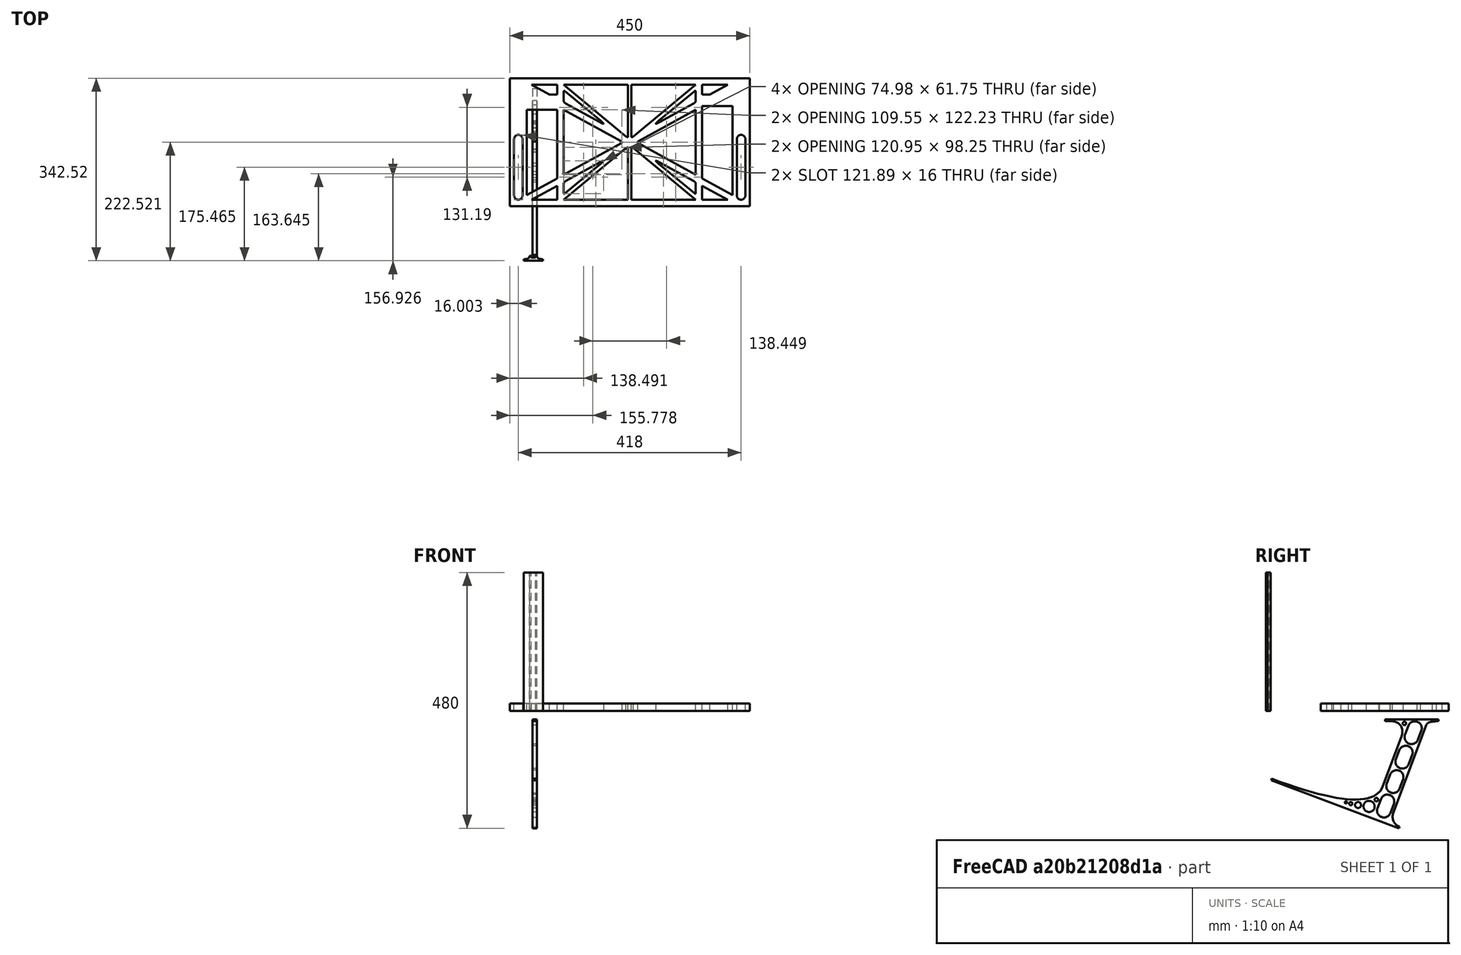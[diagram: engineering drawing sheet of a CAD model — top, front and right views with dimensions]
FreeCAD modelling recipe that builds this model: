
FCSTD DOCUMENT  (FreeCAD 0.19R0.19.2)
Label: laptopStand078
License: All rights reserved
LicenseURL: http://en.wikipedia.org/wiki/All_rights_reserved
objects: Sketcher::SketchObject×3, Part::Extrusion×3
note: 6 computed .brp shape members not serialized (recipe doc carries the construction recipe); baked Part::Feature solids carry a one-line shape summary decoded from their .brp

FEATURE [Sketcher::SketchObject] Sketch
  FullyConstrained = false
  sketch-geometry (180):
    g0: LineSegment StartX=-10.9272 StartY=-82.7794 StartZ=0 EndX=46.0728 EndY=-51.4823 EndZ=0
    g1: LineSegment StartX=366.073 StartY=-91.7794 StartZ=0 EndX=318.073 EndY=-65.424 EndZ=0
    g2: LineSegment StartX=-10.9272 StartY=77.3346 StartZ=0 EndX=-10.9272 EndY=-82.7794 EndZ=0
    g3: LineSegment StartX=375.073 StartY=-82.7794 StartZ=0 EndX=375.073 EndY=83.9235 EndZ=0
    g4: LineSegment StartX=-1.92719 StartY=-91.7794 StartZ=0 EndX=46.0728 EndY=-91.7794 EndZ=0
    g5: LineSegment StartX=318.073 StartY=124.221 StartZ=0 EndX=366.073 EndY=124.221 EndZ=0
    g6: LineSegment StartX=306.073 StartY=124.221 StartZ=0 EndX=189.124 EndY=27.0628 EndZ=0
    g7: LineSegment StartX=58.0728 StartY=-91.7794 StartZ=0 EndX=175.022 EndY=5.37834 EndZ=0
    g8: LineSegment StartX=175.022 StartY=27.0628 StartZ=0 EndX=58.0728 EndY=124.221 EndZ=0
    g9: LineSegment StartX=189.124 StartY=5.37834 StartZ=0 EndX=306.073 EndY=-91.7794 EndZ=0
    g10: LineSegment StartX=306.073 StartY=77.3346 StartZ=0 EndX=306.073 EndY=-44.8935 EndZ=0
    g11: LineSegment StartX=318.073 StartY=83.9235 StartZ=0 EndX=318.073 EndY=-51.4823 EndZ=0
    g12: LineSegment StartX=318.073 StartY=-51.4823 StartZ=0 EndX=375.073 EndY=-82.7794 EndZ=0
    g13: LineSegment StartX=318.073 StartY=-65.424 StartZ=0 EndX=318.073 EndY=-91.7794 EndZ=0
    g14: LineSegment StartX=318.073 StartY=-91.7794 StartZ=0 EndX=366.073 EndY=-91.7794 EndZ=0
    g15: LineSegment StartX=58.0728 StartY=-44.8935 StartZ=0 EndX=58.0728 EndY=77.3346 EndZ=0
    g16: LineSegment StartX=46.0728 StartY=-65.424 StartZ=0 EndX=-1.92719 EndY=-91.7794 EndZ=0
    g17: LineSegment StartX=46.0728 StartY=-65.424 StartZ=0 EndX=46.0728 EndY=-91.7794 EndZ=0
    g18: LineSegment StartX=46.0728 StartY=77.3346 StartZ=0 EndX=46.0728 EndY=-51.4823 EndZ=0
    g19: LineSegment StartX=-42.9272 StartY=136.221 StartZ=0 EndX=-42.9272 EndY=-103.779 EndZ=0
    g20: LineSegment StartX=407.073 StartY=136.221 StartZ=0 EndX=407.073 EndY=-103.779 EndZ=0
    g21: LineSegment StartX=179.022 StartY=27.0628 StartZ=0 EndX=179.022 EndY=124.221 EndZ=0
    g22: LineSegment StartX=185.124 StartY=27.0628 StartZ=0 EndX=185.124 EndY=124.221 EndZ=0
    g23: ArcOfCircle CenterX=-26.9272 CenterY=22.1087 CenterZ=0 NormalX=0 NormalY=0 NormalZ=1 AngleXU=0 Radius=8 StartAngle=1e-16 EndAngle=3.14159
    g24: ArcOfCircle CenterX=-26.9272 CenterY=-83.7794 CenterZ=0 NormalX=0 NormalY=0 NormalZ=1 AngleXU=0 Radius=8 StartAngle=3.14159 EndAngle=6.28319
    g25: LineSegment StartX=-34.9272 StartY=22.1087 StartZ=0 EndX=-34.9272 EndY=-83.7794 EndZ=0
    g26: LineSegment StartX=-18.9272 StartY=22.1087 StartZ=0 EndX=-18.9272 EndY=-83.7794 EndZ=0
    g27: LineSegment StartX=185.124 StartY=-91.7794 StartZ=0 EndX=306.073 EndY=-91.7794 EndZ=0
    g28: LineSegment StartX=179.022 StartY=-91.7794 StartZ=0 EndX=58.0728 EndY=-91.7794 EndZ=0
    g29: LineSegment StartX=306.073 StartY=124.221 StartZ=0 EndX=185.124 EndY=124.221 EndZ=0
    g30: LineSegment StartX=179.022 StartY=124.221 StartZ=0 EndX=58.0728 EndY=124.221 EndZ=0
    g31: ArcOfCircle CenterX=391.073 CenterY=22.1087 CenterZ=0 NormalX=0 NormalY=0 NormalZ=1 AngleXU=0 Radius=8 StartAngle=-4.4e-15 EndAngle=3.14159
    g32: LineSegment StartX=399.073 StartY=22.1087 StartZ=0 EndX=399.073 EndY=-83.7794 EndZ=0
    g33: LineSegment StartX=383.073 StartY=22.1087 StartZ=0 EndX=383.073 EndY=-83.7794 EndZ=0
    g34: ArcOfCircle CenterX=391.073 CenterY=-83.7794 CenterZ=0 NormalX=0 NormalY=0 NormalZ=1 AngleXU=0 Radius=8 StartAngle=3.14159 EndAngle=6.28319
    g35: Circle CenterX=175.022 CenterY=27.0628 CenterZ=0 NormalX=0 NormalY=0 NormalZ=1 AngleXU=0 Radius=1
    g36: Circle CenterX=179.022 CenterY=24.8665 CenterZ=0 NormalX=0 NormalY=0 NormalZ=1 AngleXU=0 Radius=1
    g37: Circle CenterX=179.022 CenterY=27.0628 CenterZ=0 NormalX=0 NormalY=0 NormalZ=1 AngleXU=0 Radius=1
    g38: BSplineCurve PolesCount=3 KnotsCount=2 Degree=2 IsPeriodic=0
    g39: GeomPoint X=175.022 Y=27.0628 Z=0
    g40: GeomPoint X=179.022 Y=27.0628 Z=0
    g41: Circle CenterX=189.124 CenterY=27.0628 CenterZ=0 NormalX=0 NormalY=0 NormalZ=1 AngleXU=0 Radius=1
    g42: Circle CenterX=185.124 CenterY=24.8665 CenterZ=0 NormalX=0 NormalY=0 NormalZ=1 AngleXU=0 Radius=1
    g43: Circle CenterX=185.124 CenterY=27.0628 CenterZ=0 NormalX=0 NormalY=0 NormalZ=1 AngleXU=0 Radius=1
    g44: BSplineCurve PolesCount=3 KnotsCount=2 Degree=2 IsPeriodic=0
    g45: GeomPoint X=189.124 Y=27.0628 Z=0
    g46: GeomPoint X=185.124 Y=27.0628 Z=0
    g47: Circle CenterX=175.022 CenterY=5.37834 CenterZ=0 NormalX=0 NormalY=0 NormalZ=1 AngleXU=0 Radius=1
    g48: Circle CenterX=179.022 CenterY=7.57463 CenterZ=0 NormalX=0 NormalY=0 NormalZ=1 AngleXU=0 Radius=1
    g49: Circle CenterX=179.022 CenterY=5.34704 CenterZ=0 NormalX=0 NormalY=0 NormalZ=1 AngleXU=0 Radius=1
    g50: BSplineCurve PolesCount=3 KnotsCount=2 Degree=2 IsPeriodic=0
    g51: GeomPoint X=175.022 Y=5.37834 Z=0
    g52: GeomPoint X=179.022 Y=5.34704 Z=0
    g53: Circle CenterX=189.124 CenterY=5.37834 CenterZ=0 NormalX=0 NormalY=0 NormalZ=1 AngleXU=0 Radius=1
    g54: Circle CenterX=185.124 CenterY=7.57463 CenterZ=0 NormalX=0 NormalY=0 NormalZ=1 AngleXU=0 Radius=1
    g55: Circle CenterX=185.124 CenterY=5.34704 CenterZ=0 NormalX=0 NormalY=0 NormalZ=1 AngleXU=0 Radius=1
    g56: BSplineCurve PolesCount=3 KnotsCount=2 Degree=2 IsPeriodic=0
    g57: GeomPoint X=189.124 Y=5.37834 Z=0
    g58: GeomPoint X=185.124 Y=5.34704 Z=0
    g59: LineSegment StartX=179.022 StartY=5.34704 StartZ=0 EndX=179.022 EndY=-91.7794 EndZ=0
    g60: LineSegment StartX=185.124 StartY=-91.7794 StartZ=0 EndX=185.124 EndY=5.34704 EndZ=0
    g61: Circle CenterX=165.871 CenterY=18.1458 CenterZ=0 NormalX=0 NormalY=0 NormalZ=1 AngleXU=0 Radius=1
    g62: Circle CenterX=169.377 CenterY=16.2206 CenterZ=0 NormalX=0 NormalY=0 NormalZ=1 AngleXU=0 Radius=1
    g63: Circle CenterX=165.871 CenterY=14.2954 CenterZ=0 NormalX=0 NormalY=0 NormalZ=1 AngleXU=0 Radius=1
    g64: BSplineCurve PolesCount=3 KnotsCount=2 Degree=2 IsPeriodic=0
    g65: GeomPoint X=165.871 Y=18.1458 Z=0
    g66: GeomPoint X=165.871 Y=14.2954 Z=0
    g67: Circle CenterX=198.275 CenterY=18.1458 CenterZ=0 NormalX=0 NormalY=0 NormalZ=1 AngleXU=0 Radius=1
    g68: Circle CenterX=194.768 CenterY=16.2206 CenterZ=0 NormalX=0 NormalY=0 NormalZ=1 AngleXU=0 Radius=1
    g69: Circle CenterX=198.275 CenterY=14.2954 CenterZ=0 NormalX=0 NormalY=0 NormalZ=1 AngleXU=0 Radius=1
    g70: BSplineCurve PolesCount=3 KnotsCount=2 Degree=2 IsPeriodic=0
    g71: GeomPoint X=198.275 Y=18.1458 Z=0
    g72: GeomPoint X=198.275 Y=14.2954 Z=0
    g73: LineSegment StartX=165.871 StartY=18.1458 StartZ=0 EndX=58.0728 EndY=77.3346 EndZ=0
    g74: LineSegment StartX=58.0728 StartY=-44.8935 StartZ=0 EndX=165.871 EndY=14.2954 EndZ=0
    g75: LineSegment StartX=198.275 StartY=18.1458 StartZ=0 EndX=306.073 EndY=77.3346 EndZ=0
    g76: LineSegment StartX=198.275 StartY=14.2954 StartZ=0 EndX=306.073 EndY=-44.8935 EndZ=0
    g77: LineSegment StartX=407.073 StartY=-103.779 StartZ=0 EndX=-42.9272 EndY=-103.779 EndZ=0
    g78: LineSegment StartX=407.073 StartY=136.221 StartZ=0 EndX=-42.9272 EndY=136.221 EndZ=0
    g79: LineSegment StartX=46.0728 StartY=77.3346 StartZ=0 EndX=-10.9272 EndY=77.3346 EndZ=0
    g80: LineSegment StartX=46.0728 StartY=105.865 StartZ=0 EndX=31.5028 EndY=105.865 EndZ=0
    g81: LineSegment StartX=46.0728 StartY=124.221 StartZ=0 EndX=46.0728 EndY=105.865 EndZ=0
    g82: LineSegment StartX=-1.92719 StartY=124.221 StartZ=0 EndX=31.5028 EndY=105.865 EndZ=0
    g83: LineSegment StartX=46.0728 StartY=124.221 StartZ=0 EndX=-1.92719 EndY=124.221 EndZ=0
    g84: LineSegment StartX=318.073 StartY=83.9235 StartZ=0 EndX=375.073 EndY=83.9235 EndZ=0
    g85: LineSegment StartX=318.073 StartY=105.865 StartZ=0 EndX=332.643 EndY=105.865 EndZ=0
    g86: LineSegment StartX=332.643 StartY=105.865 StartZ=0 EndX=366.073 EndY=124.221 EndZ=0
    g87: LineSegment StartX=318.073 StartY=124.221 StartZ=0 EndX=318.073 EndY=105.865 EndZ=0
    g88: Circle CenterX=125.607 CenterY=54.1951 CenterZ=0 NormalX=0 NormalY=0 NormalZ=1 AngleXU=0 Radius=1
    g89: Circle CenterX=139.632 CenterY=46.4944 CenterZ=0 NormalX=0 NormalY=0 NormalZ=1 AngleXU=0 Radius=1
    g90: Circle CenterX=127.326 CenterY=56.7187 CenterZ=0 NormalX=0 NormalY=0 NormalZ=1 AngleXU=0 Radius=1
    g91: BSplineCurve PolesCount=3 KnotsCount=2 Degree=2 IsPeriodic=0
    g92: GeomPoint X=125.607 Y=54.1951 Z=0
    g93: GeomPoint X=127.326 Y=56.7187 Z=0
    g94: Circle CenterX=236.821 CenterY=56.7187 CenterZ=0 NormalX=0 NormalY=0 NormalZ=1 AngleXU=0 Radius=1
    g95: Circle CenterX=224.513 CenterY=46.4944 CenterZ=0 NormalX=0 NormalY=0 NormalZ=1 AngleXU=0 Radius=1
    g96: Circle CenterX=238.538 CenterY=54.1951 CenterZ=0 NormalX=0 NormalY=0 NormalZ=1 AngleXU=0 Radius=1
    g97: BSplineCurve PolesCount=3 KnotsCount=2 Degree=2 IsPeriodic=0
    g98: GeomPoint X=236.821 Y=56.7187 Z=0
    g99: GeomPoint X=238.538 Y=54.1951 Z=0
    g100: Circle CenterX=238.538 CenterY=-21.7539 CenterZ=0 NormalX=0 NormalY=0 NormalZ=1 AngleXU=0 Radius=1
    g101: Circle CenterX=224.513 CenterY=-14.0532 CenterZ=0 NormalX=0 NormalY=0 NormalZ=1 AngleXU=0 Radius=1
    g102: Circle CenterX=236.821 CenterY=-24.2775 CenterZ=0 NormalX=0 NormalY=0 NormalZ=1 AngleXU=0 Radius=1
    g103: BSplineCurve PolesCount=3 KnotsCount=2 Degree=2 IsPeriodic=0
    g104: GeomPoint X=238.538 Y=-21.7539 Z=0
    g105: GeomPoint X=236.821 Y=-24.2775 Z=0
    g106: Circle CenterX=125.607 CenterY=-21.7539 CenterZ=0 NormalX=0 NormalY=0 NormalZ=1 AngleXU=0 Radius=1
    g107: Circle CenterX=139.632 CenterY=-14.0532 CenterZ=0 NormalX=0 NormalY=0 NormalZ=1 AngleXU=0 Radius=1
    g108: Circle CenterX=127.325 CenterY=-24.2775 CenterZ=0 NormalX=0 NormalY=0 NormalZ=1 AngleXU=0 Radius=1
    g109: BSplineCurve PolesCount=3 KnotsCount=2 Degree=2 IsPeriodic=0
    g110: GeomPoint X=125.607 Y=-21.7539 Z=0
    g111: GeomPoint X=127.325 Y=-24.2775 Z=0
    g112: Circle CenterX=302.996 CenterY=111.695 CenterZ=0 NormalX=0 NormalY=0 NormalZ=1 AngleXU=0 Radius=1
    g113: Circle CenterX=306.073 CenterY=114.251 CenterZ=0 NormalX=0 NormalY=0 NormalZ=1 AngleXU=0 Radius=1
    g114: Circle CenterX=306.073 CenterY=110.251 CenterZ=0 NormalX=0 NormalY=0 NormalZ=1 AngleXU=0 Radius=1
    g115: BSplineCurve PolesCount=3 KnotsCount=2 Degree=2 IsPeriodic=0
    g116: GeomPoint X=302.996 Y=111.695 Z=0
    g117: GeomPoint X=306.073 Y=110.251 Z=0
    g118: Circle CenterX=306.073 CenterY=95.2763 CenterZ=0 NormalX=0 NormalY=0 NormalZ=1 AngleXU=0 Radius=1
    g119: Circle CenterX=306.073 CenterY=91.2763 CenterZ=0 NormalX=0 NormalY=0 NormalZ=1 AngleXU=0 Radius=1
    g120: Circle CenterX=302.567 CenterY=89.3511 CenterZ=0 NormalX=0 NormalY=0 NormalZ=1 AngleXU=0 Radius=1
    g121: BSplineCurve PolesCount=3 KnotsCount=2 Degree=2 IsPeriodic=0
    g122: GeomPoint X=306.073 Y=95.2763 Z=0
    g123: GeomPoint X=302.567 Y=89.3511 Z=0
    g124: LineSegment StartX=306.073 StartY=110.251 StartZ=0 EndX=306.073 EndY=95.2763 EndZ=0
    g125: LineSegment StartX=302.996 StartY=111.695 StartZ=0 EndX=236.821 EndY=56.7187 EndZ=0
    g126: LineSegment StartX=238.538 StartY=54.1951 StartZ=0 EndX=302.567 EndY=89.3511 EndZ=0
    g127: Circle CenterX=61.1496 CenterY=111.695 CenterZ=0 NormalX=0 NormalY=0 NormalZ=1 AngleXU=0 Radius=1
    g128: Circle CenterX=58.0728 CenterY=114.251 CenterZ=0 NormalX=0 NormalY=0 NormalZ=1 AngleXU=0 Radius=1
    g129: Circle CenterX=58.0728 CenterY=110.251 CenterZ=0 NormalX=0 NormalY=0 NormalZ=1 AngleXU=0 Radius=1
    g130: BSplineCurve PolesCount=3 KnotsCount=2 Degree=2 IsPeriodic=0
    g131: GeomPoint X=61.1496 Y=111.695 Z=0
    g132: GeomPoint X=58.0728 Y=110.251 Z=0
    g133: Circle CenterX=61.5791 CenterY=89.3511 CenterZ=0 NormalX=0 NormalY=0 NormalZ=1 AngleXU=0 Radius=1
    g134: Circle CenterX=58.0728 CenterY=91.2763 CenterZ=0 NormalX=0 NormalY=0 NormalZ=1 AngleXU=0 Radius=1
    g135: Circle CenterX=58.0728 CenterY=95.2763 CenterZ=0 NormalX=0 NormalY=0 NormalZ=1 AngleXU=0 Radius=1
    g136: BSplineCurve PolesCount=3 KnotsCount=2 Degree=2 IsPeriodic=0
    g137: GeomPoint X=61.5791 Y=89.3511 Z=0
    g138: GeomPoint X=58.0728 Y=95.2763 Z=0
    g139: LineSegment StartX=58.0728 StartY=110.251 StartZ=0 EndX=58.0728 EndY=95.2763 EndZ=0
    g140: LineSegment StartX=61.1496 StartY=111.695 StartZ=0 EndX=127.326 EndY=56.7187 EndZ=0
    g141: LineSegment StartX=125.607 StartY=54.1951 StartZ=0 EndX=61.5791 EndY=89.3511 EndZ=0
    g142: Circle CenterX=61.5791 CenterY=-56.9099 CenterZ=0 NormalX=0 NormalY=0 NormalZ=1 AngleXU=0 Radius=1
    g143: Circle CenterX=58.0728 CenterY=-58.8351 CenterZ=0 NormalX=0 NormalY=0 NormalZ=1 AngleXU=0 Radius=1
    g144: Circle CenterX=58.0728 CenterY=-62.8351 CenterZ=0 NormalX=0 NormalY=0 NormalZ=1 AngleXU=0 Radius=1
    g145: BSplineCurve PolesCount=3 KnotsCount=2 Degree=2 IsPeriodic=0
    g146: GeomPoint X=61.5791 Y=-56.9099 Z=0
    g147: GeomPoint X=58.0728 Y=-62.8351 Z=0
    g148: Circle CenterX=58.0728 CenterY=-77.8102 CenterZ=0 NormalX=0 NormalY=0 NormalZ=1 AngleXU=0 Radius=1
    g149: Circle CenterX=58.0728 CenterY=-81.8102 CenterZ=0 NormalX=0 NormalY=0 NormalZ=1 AngleXU=0 Radius=1
    g150: Circle CenterX=61.1496 CenterY=-79.2541 CenterZ=0 NormalX=0 NormalY=0 NormalZ=1 AngleXU=0 Radius=1
    g151: BSplineCurve PolesCount=3 KnotsCount=2 Degree=2 IsPeriodic=0
    g152: GeomPoint X=58.0728 Y=-77.8102 Z=0
    g153: GeomPoint X=61.1496 Y=-79.2541 Z=0
    g154: LineSegment StartX=58.0728 StartY=-62.8351 StartZ=0 EndX=58.0728 EndY=-77.8102 EndZ=0
    g155: LineSegment StartX=61.1496 StartY=-79.2541 StartZ=0 EndX=127.325 EndY=-24.2775 EndZ=0
    g156: LineSegment StartX=125.607 StartY=-21.7539 StartZ=0 EndX=61.5791 EndY=-56.9099 EndZ=0
    g157: Circle CenterX=302.567 CenterY=-56.9099 CenterZ=0 NormalX=0 NormalY=0 NormalZ=1 AngleXU=0 Radius=1
    g158: Circle CenterX=306.073 CenterY=-58.8351 CenterZ=0 NormalX=0 NormalY=0 NormalZ=1 AngleXU=0 Radius=1
    g159: Circle CenterX=306.073 CenterY=-62.8351 CenterZ=0 NormalX=0 NormalY=0 NormalZ=1 AngleXU=0 Radius=1
    g160: BSplineCurve PolesCount=3 KnotsCount=2 Degree=2 IsPeriodic=0
    g161: GeomPoint X=302.567 Y=-56.9099 Z=0
    g162: GeomPoint X=306.073 Y=-62.8351 Z=0
    g163: Circle CenterX=302.996 CenterY=-79.2541 CenterZ=0 NormalX=0 NormalY=0 NormalZ=1 AngleXU=0 Radius=1
    g164: Circle CenterX=306.073 CenterY=-81.8102 CenterZ=0 NormalX=0 NormalY=0 NormalZ=1 AngleXU=0 Radius=1
    g165: Circle CenterX=306.073 CenterY=-77.8102 CenterZ=0 NormalX=0 NormalY=0 NormalZ=1 AngleXU=0 Radius=1
    g166: BSplineCurve PolesCount=3 KnotsCount=2 Degree=2 IsPeriodic=0
    g167: GeomPoint X=302.996 Y=-79.2541 Z=0
    g168: GeomPoint X=306.073 Y=-77.8102 Z=0
    g169: LineSegment StartX=306.073 StartY=-62.8351 StartZ=0 EndX=306.073 EndY=-77.8102 EndZ=0
    g170: LineSegment StartX=302.996 StartY=-79.2541 StartZ=0 EndX=236.821 EndY=-24.2775 EndZ=0
    g171: LineSegment StartX=238.538 StartY=-21.7539 StartZ=0 EndX=302.567 EndY=-56.9099 EndZ=0
    g172: LineSegment StartX=58.0728 StartY=-91.7794 StartZ=0 EndX=63.9135 EndY=-91.7794 EndZ=0
    g173: LineSegment StartX=58.0728 StartY=-91.7794 StartZ=0 EndX=61.6457 EndY=-88.8112 EndZ=0
    g174: LineSegment StartX=179.022 StartY=-91.7794 StartZ=0 EndX=171.895 EndY=-91.7794 EndZ=0
    g175: LineSegment StartX=179.022 StartY=-91.7794 StartZ=0 EndX=179.022 EndY=-85.8163 EndZ=0
    g176: LineSegment StartX=185.124 StartY=-91.7794 StartZ=0 EndX=185.124 EndY=-86.2028 EndZ=0
    g177: LineSegment StartX=185.124 StartY=-91.7794 StartZ=0 EndX=191.747 EndY=-91.7794 EndZ=0
    g178: LineSegment StartX=306.073 StartY=-91.7794 StartZ=0 EndX=298.776 EndY=-91.7794 EndZ=0
    g179: LineSegment StartX=306.073 StartY=-91.7794 StartZ=0 EndX=299.888 EndY=-86.6416 EndZ=0
  constraints (316):
    c: Horizontal(g4)
    c: Horizontal(g5)
    c: Coincident(g11,g12)
    c: Coincident(g13,g1)
    c: Tangent(g11,g13)
    c: Coincident(g17,g16)
    c: Coincident(g0,g18)
    c: Block(g8)
    c: Block(g6)
    c: Block(g12)
    c: Block(g3)
    c: Block(g1)
    c: Block(g13)
    c: Block(g9)
    c: Block(g7)
    c: Block(g17)
    c: Block(g16)
    c: Block(g0)
    c: Block(g2)
    c: Block(g10)
    c: Block(g5)
    c: Block(g14)
    c: Block(g4)
    c: Vertical(g19)
    c: Vertical(g20)
    c: Block(g20)
    c: Block(g19)
    c: Vertical(g21)
    c: Vertical(g22)
    c: Block(g21)
    c: Block(g22)
    c: Tangent(g23,g26) = 1.5708
    c: Tangent(g23,g25) = -1.5708
    c: Tangent(g25,g24) = -1.5708
    c: Tangent(g26,g24) = 1.5708
    c: Vertical(g25)
    c: Equal(g23,g24)
    c: Block(g26)
    c: Block(g25)
    c: Coincident(g27,g9)
    c: Horizontal(g27)
    c: Coincident(g28,g7)
    c: Horizontal(g28)
    c: Coincident(g29,g6)
    c: Coincident(g29,g22)
    c: Horizontal(g29)
    c: Coincident(g30,g21)
    c: Coincident(g30,g8)
    c: Horizontal(g30)
    c: Tangent(g31,g32) = 1.5708
    c: Tangent(g32,g34) = 1.5708
    c: Equal(g31,g34)
    c: Coincident(g33,g31)
    c: Coincident(g33,g34)
    c: Block(g32)
    c: Block(g33)
    c: Coincident(g38,g8)
    c: Weight(g35) = 1
    c: Equal(g35,g36)
    c: Equal(g35,g37)
    c: Coincident(g38,g21)
    c: InternalAlignment(g35,g38)
    c: InternalAlignment(g36,g38)
    c: InternalAlignment(g37,g38)
    c: InternalAlignment(g39,g38)
    c: InternalAlignment(g40,g38)
    c: Coincident(g44,g6)
    c: Weight(g41) = 1
    c: Equal(g41,g42)
    c: Equal(g41,g43)
    c: Coincident(g44,g22)
    c: InternalAlignment(g41,g44)
    c: InternalAlignment(g42,g44)
    c: InternalAlignment(g43,g44)
    c: InternalAlignment(g45,g44)
    c: InternalAlignment(g46,g44)
    c: Block(g44)
    c: Block(g38)
    c: Coincident(g50,g7)
    c: Weight(g47) = 1
    c: Equal(g47,g48)
    c: Equal(g47,g49)
    c: InternalAlignment(g47,g50)
    c: InternalAlignment(g48,g50)
    c: InternalAlignment(g49,g50)
    c: InternalAlignment(g51,g50)
    c: InternalAlignment(g52,g50)
    c: Weight(g53) = 1
    c: Equal(g53,g54)
    c: Equal(g53,g55)
    c: InternalAlignment(g53,g56)
    c: InternalAlignment(g54,g56)
    c: InternalAlignment(g55,g56)
    c: InternalAlignment(g57,g56)
    c: InternalAlignment(g58,g56)
    c: Block(g56)
    c: Block(g50)
    c: Coincident(g59,g50)
    c: Coincident(g59,g28)
    c: Vertical(g59)
    c: Coincident(g60,g27)
    c: Coincident(g60,g56)
    c: Vertical(g60)
    c: Weight(g61) = 1
    c: Equal(g61,g62)
    c: Equal(g61,g63)
    c: InternalAlignment(g61,g64)
    c: InternalAlignment(g62,g64)
    c: InternalAlignment(g63,g64)
    c: InternalAlignment(g65,g64)
    c: InternalAlignment(g66,g64)
    c: Weight(g67) = 1
    c: Equal(g67,g68)
    c: Equal(g67,g69)
    c: InternalAlignment(g67,g70)
    c: InternalAlignment(g68,g70)
    c: InternalAlignment(g69,g70)
    c: InternalAlignment(g71,g70)
    c: InternalAlignment(g72,g70)
    c: Block(g64)
    c: Block(g70)
    c: Coincident(g73,g64)
    c: Coincident(g73,g15)
    c: Coincident(g74,g15)
    c: Coincident(g74,g64)
    c: Coincident(g75,g70)
    c: Coincident(g75,g10)
    c: Coincident(g76,g70)
    c: Coincident(g76,g10)
    c: Block(g15)
    c: Coincident(g77,g20)
    c: Coincident(g77,g19)
    c: Horizontal(g77)
    c: Distance(g77) = 450
    c: Coincident(g78,g20)
    c: Coincident(g78,g19)
    c: Horizontal(g78)
    c: Horizontal(g79)
    c: Coincident(g18,g79)
    c: Horizontal(g80)
    c: Vertical(g81)
    c: Block(g81)
    c: Block(g80)
    c: Block(g79)
    c: Distance(g81) = 18.3554
    c: Coincident(g83,g81)
    c: Coincident(g83,g82)
    c: Horizontal(g83)
    c: Block(g83)
    c: Block(g82)
    c: Coincident(g80,g82)
    c: Coincident(g2,g79)
    c: Coincident(g84,g11)
    c: Horizontal(g84)
    c: Horizontal(g85)
    c: Block(g84)
    c: Coincident(g86,g5)
    c: Coincident(g87,g5)
    c: Coincident(g87,g85)
    c: Vertical(g87)
    c: Block(g87)
    c: Coincident(g85,g86)
    c: Block(g86)
    c: Coincident(g3,g84)
    c: Weight(g88) = 1
    c: Equal(g88,g89)
    c: Equal(g88,g90)
    c: InternalAlignment(g88,g91)
    c: InternalAlignment(g89,g91)
    c: InternalAlignment(g90,g91)
    c: InternalAlignment(g92,g91)
    c: InternalAlignment(g93,g91)
    c: Block(g91)
    c: Weight(g94) = 1
    c: Equal(g94,g95)
    c: Equal(g94,g96)
    c: InternalAlignment(g94,g97)
    c: InternalAlignment(g95,g97)
    c: InternalAlignment(g96,g97)
    c: InternalAlignment(g98,g97)
    c: InternalAlignment(g99,g97)
    c: Block(g97)
    c: Weight(g100) = 1
    c: Equal(g100,g101)
    c: Equal(g100,g102)
    c: InternalAlignment(g100,g103)
    c: InternalAlignment(g101,g103)
    c: InternalAlignment(g102,g103)
    c: InternalAlignment(g104,g103)
    c: InternalAlignment(g105,g103)
    c: Block(g103)
    c: Weight(g106) = 1
    c: Equal(g106,g107)
    c: Equal(g106,g108)
    c: InternalAlignment(g106,g109)
    c: InternalAlignment(g107,g109)
    c: InternalAlignment(g108,g109)
    c: InternalAlignment(g110,g109)
    c: InternalAlignment(g111,g109)
    c: Block(g109)
    c: Weight(g112) = 1
    c: Equal(g112,g113)
    c: Equal(g112,g114)
    c: InternalAlignment(g112,g115)
    c: InternalAlignment(g113,g115)
    c: InternalAlignment(g114,g115)
    c: InternalAlignment(g116,g115)
    c: InternalAlignment(g117,g115)
    c: Weight(g118) = 1
    c: Equal(g118,g119)
    c: Equal(g118,g120)
    c: InternalAlignment(g118,g121)
    c: InternalAlignment(g119,g121)
    c: InternalAlignment(g120,g121)
    c: InternalAlignment(g122,g121)
    c: InternalAlignment(g123,g121)
    c: Block(g115)
    c: Block(g121)
    c: Coincident(g124,g115)
    c: Coincident(g124,g121)
    c: Vertical(g124)
    c: Coincident(g125,g115)
    c: Coincident(g125,g97)
    c: Coincident(g126,g97)
    c: Coincident(g126,g121)
    c: Weight(g127) = 1
    c: Equal(g127,g128)
    c: Equal(g127,g129)
    c: InternalAlignment(g127,g130)
    c: InternalAlignment(g128,g130)
    c: InternalAlignment(g129,g130)
    c: InternalAlignment(g131,g130)
    c: InternalAlignment(g132,g130)
    c: Weight(g133) = 1
    c: Equal(g133,g134)
    c: Equal(g133,g135)
    c: InternalAlignment(g133,g136)
    c: InternalAlignment(g134,g136)
    c: InternalAlignment(g135,g136)
    c: InternalAlignment(g137,g136)
    c: InternalAlignment(g138,g136)
    c: Block(g130)
    c: Block(g136)
    c: Coincident(g139,g130)
    c: Coincident(g139,g136)
    c: Vertical(g139)
    c: Coincident(g140,g130)
    c: Coincident(g140,g91)
    c: Coincident(g141,g91)
    c: Coincident(g141,g136)
    c: Weight(g142) = 1
    c: Equal(g142,g143)
    c: Equal(g142,g144)
    c: InternalAlignment(g142,g145)
    c: InternalAlignment(g143,g145)
    c: InternalAlignment(g144,g145)
    c: InternalAlignment(g146,g145)
    c: InternalAlignment(g147,g145)
    c: Weight(g148) = 1
    c: Equal(g148,g149)
    c: Equal(g148,g150)
    c: InternalAlignment(g148,g151)
    c: InternalAlignment(g149,g151)
    c: InternalAlignment(g150,g151)
    c: InternalAlignment(g152,g151)
    c: InternalAlignment(g153,g151)
    c: Block(g145)
    c: Block(g151)
    c: Coincident(g154,g145)
    c: Coincident(g154,g151)
    c: Vertical(g154)
    c: Coincident(g155,g151)
    c: Coincident(g155,g109)
    c: Coincident(g156,g109)
    c: Coincident(g156,g145)
    c: Weight(g157) = 1
    c: Equal(g157,g158)
    c: Equal(g157,g159)
    c: InternalAlignment(g157,g160)
    c: InternalAlignment(g158,g160)
    c: InternalAlignment(g159,g160)
    c: InternalAlignment(g161,g160)
    c: InternalAlignment(g162,g160)
    c: Weight(g163) = 1
    c: Equal(g163,g164)
    c: Equal(g163,g165)
    c: InternalAlignment(g163,g166)
    c: InternalAlignment(g164,g166)
    c: InternalAlignment(g165,g166)
    c: InternalAlignment(g167,g166)
    c: InternalAlignment(g168,g166)
    c: Block(g160)
    c: Block(g166)
    c: Coincident(g169,g160)
    c: Coincident(g169,g166)
    c: Vertical(g169)
    c: Coincident(g170,g166)
    c: Coincident(g170,g103)
    c: Coincident(g171,g103)
    c: Coincident(g171,g160)
    c: Horizontal(g172)
    c: Horizontal(g174)
    c: Vertical(g175)
    c: Vertical(g176)
    c: Horizontal(g177)
    c: Horizontal(g178)
    c: Parallel(g7,g173)
    c: Parallel(g9,g179)
    c: Coincident(g179,g9)
    c: Coincident(g178,g9)
    c: Coincident(g176,g27)
    c: Coincident(g177,g27)
    c: Coincident(g28,g175)
    c: Coincident(g174,g28)
    c: Coincident(g173,g7)
    c: Coincident(g172,g7)
FEATURE [Sketcher::SketchObject] Sketch001
  FullyConstrained = true
  MapMode = 4
  Placement = pos=(0,0,0) rot=(0.57735,0.57735,0.57735;2.0944rad)
  Support = -> [Sketch]
  sketch-geometry (46):
    g0: BSplineCurve PolesCount=3 KnotsCount=2 Degree=2 IsPeriodic=0
    g1: ArcOfCircle CenterX=73.1223 CenterY=-32.291 CenterZ=0 NormalX=0 NormalY=0 NormalZ=1 AngleXU=0 Radius=13 StartAngle=5.92268 EndAngle=9.06428
    g2: ArcOfCircle CenterX=66.7816 CenterY=-49.1439 CenterZ=0 NormalX=0 NormalY=0 NormalZ=1 AngleXU=0 Radius=13 StartAngle=2.78068 EndAngle=5.92131
    g3: ArcOfCircle CenterX=55.9263 CenterY=-78.1807 CenterZ=0 NormalX=0 NormalY=0 NormalZ=1 AngleXU=0 Radius=13 StartAngle=5.92268 EndAngle=9.06428
    g4: ArcOfCircle CenterX=49.5884 CenterY=-95.0342 CenterZ=0 NormalX=0 NormalY=0 NormalZ=1 AngleXU=0 Radius=13 StartAngle=2.78068 EndAngle=5.92131
    g5: ArcOfCircle CenterX=38.7206 CenterY=-124.067 CenterZ=0 NormalX=0 NormalY=0 NormalZ=1 AngleXU=0 Radius=13 StartAngle=5.92268 EndAngle=9.06428
    g6: ArcOfCircle CenterX=32.3875 CenterY=-140.92 CenterZ=0 NormalX=0 NormalY=0 NormalZ=1 AngleXU=0 Radius=13 StartAngle=2.78068 EndAngle=5.92131
    g7: ArcOfCircle CenterX=21.4715 CenterY=-169.934 CenterZ=0 NormalX=0 NormalY=0 NormalZ=1 AngleXU=0 Radius=13 StartAngle=5.92268 EndAngle=9.06428
    g8: ArcOfCircle CenterX=15.1336 CenterY=-186.787 CenterZ=0 NormalX=0 NormalY=0 NormalZ=1 AngleXU=0 Radius=13 StartAngle=2.78068 EndAngle=5.92131
    g9-g12: Circle x4 (B-spline internal-alignment scaffolding for g13; pole/knot coordinates omitted)
    g13: BSplineCurve PolesCount=4 KnotsCount=2 Degree=3 IsPeriodic=0
    g14: GeomPoint X=28.8094 Y=-19.0875 Z=0
    g15: GeomPoint X=47.0443 Y=-50.4712 Z=0
    g16: Circle CenterX=53.5586 CenterY=-23.2695 CenterZ=0 NormalX=0 NormalY=0 NormalZ=1 AngleXU=0 Radius=3.24518
    g17: Circle CenterX=-195.441 CenterY=-127.082 CenterZ=0 NormalX=0 NormalY=0 NormalZ=1 AngleXU=0 Radius=1
    g18: Circle CenterX=-8.24091 CenterY=-197.481 CenterZ=0 NormalX=0 NormalY=0 NormalZ=1 AngleXU=0 Radius=1
    g19: Circle CenterX=12.8789 CenterY=-141.321 CenterZ=0 NormalX=0 NormalY=0 NormalZ=1 AngleXU=0 Radius=1
    g20: BSplineCurve PolesCount=3 KnotsCount=2 Degree=2 IsPeriodic=0
    g21: GeomPoint X=-195.441 Y=-127.082 Z=0
    g22: GeomPoint X=12.8789 Y=-141.321 Z=0
    g23: Circle CenterX=-12.8016 CenterY=-179.036 CenterZ=0 NormalX=0 NormalY=0 NormalZ=1 AngleXU=0 Radius=10.5072
    g24: Circle CenterX=0.933922 CenterY=-166.43 CenterZ=0 NormalX=0 NormalY=0 NormalZ=1 AngleXU=0 Radius=3.26661
    g25: Circle CenterX=-33.5518 CenterY=-176.44 CenterZ=0 NormalX=0 NormalY=0 NormalZ=1 AngleXU=0 Radius=5.64388
    g26: Circle CenterX=-47.2366 CenterY=-173.859 CenterZ=0 NormalX=0 NormalY=0 NormalZ=1 AngleXU=0 Radius=3.01653
    g27: Circle CenterX=-56.2595 CenterY=-171.456 CenterZ=0 NormalX=0 NormalY=0 NormalZ=1 AngleXU=0 Radius=2.12826
    g28: ArcOfCircle CenterX=51.2151 CenterY=-198.473 CenterZ=0 NormalX=0 NormalY=0 NormalZ=1 AngleXU=0 Radius=20 StartAngle=2.78189 EndAngle=4.35269
    g29: LineSegment StartX=32.4951 StartY=-191.433 StartZ=0 EndX=94.6578 EndY=-26.1352 EndZ=0
    g30: LineSegment StartX=43.1192 StartY=-220.001 StartZ=0 EndX=-196.497 EndY=-129.89 EndZ=0
    g31: LineSegment StartX=43.1192 StartY=-220.001 StartZ=0 EndX=44.1752 EndY=-217.193 EndZ=0
    g32: LineSegment StartX=117.223 StartY=-19.0875 StartZ=0 EndX=117.223 EndY=-16.0875 EndZ=0
    g33: LineSegment StartX=117.223 StartY=-16.0875 StartZ=0 EndX=17.2232 EndY=-16.0875 EndZ=0
    g34: LineSegment StartX=17.2232 StartY=-16.0875 StartZ=0 EndX=17.2232 EndY=-19.0875 EndZ=0
    g35: LineSegment StartX=28.8094 StartY=-19.0875 StartZ=0 EndX=17.2232 EndY=-19.0875 EndZ=0
    g36: LineSegment StartX=47.0443 StartY=-50.4712 StartZ=0 EndX=12.8789 EndY=-141.321 EndZ=0
    g37: LineSegment StartX=-195.441 StartY=-127.082 StartZ=0 EndX=-196.497 EndY=-129.89 EndZ=0
    g38: LineSegment StartX=85.2866 StartY=-36.8766 StartZ=0 EndX=78.9396 EndY=-53.7463 EndZ=0
    g39: LineSegment StartX=60.9579 StartY=-27.7053 StartZ=0 EndX=54.6191 EndY=-44.5532 EndZ=0
    g40: LineSegment StartX=68.0907 StartY=-82.7664 StartZ=0 EndX=61.7465 EndY=-99.6365 EndZ=0
    g41: LineSegment StartX=43.7619 StartY=-73.595 StartZ=0 EndX=37.426 EndY=-90.4435 EndZ=0
    g42: LineSegment StartX=50.885 StartY=-128.652 StartZ=0 EndX=44.5456 EndY=-145.522 EndZ=0
    g43: LineSegment StartX=26.5562 StartY=-119.481 StartZ=0 EndX=20.2251 EndY=-136.329 EndZ=0
    g44: LineSegment StartX=9.3071 StartY=-165.349 StartZ=0 EndX=2.97115 EndY=-182.197 EndZ=0
    g45: LineSegment StartX=33.6358 StartY=-174.52 StartZ=0 EndX=27.2917 EndY=-191.39 EndZ=0
  constraints (71):
    c: Block(g0)
    c: Block(g1)
    c: Block(g2)
    c: Block(g4)
    c: Block(g3)
    c: Block(g6)
    c: Block(g5)
    c: Block(g8)
    c: Block(g7)
    c: Weight(g9) = 1
    c: Equal(g9,g10)
    c: Equal(g9,g11)
    c: Equal(g9,g12)
    c: InternalAlignment(g9-g12 -> g13) x4
    c: InternalAlignment(g14,g13)
    c: InternalAlignment(g15,g13)
    c: Block(g16)
    c: Weight(g17) = 1
    c: Equal(g17,g18)
    c: Equal(g17,g19)
    c: InternalAlignment(g17,g20)
    c: InternalAlignment(g18,g20)
    c: InternalAlignment(g19,g20)
    c: InternalAlignment(g21,g20)
    c: InternalAlignment(g22,g20)
    c: Block(g20)
    c: Block(g23)
    c: Block(g24)
    c: Block(g25)
    c: Block(g26)
    c: Block(g27)
    c: Block(g28)
    c: Coincident(g29,g28)
    c: Coincident(g29,g0)
    c: Block(g13)
    c: Coincident(g31,g30)
    c: Coincident(g31,g28)
    c: Block(g31)
    c: Coincident(g32,g0)
    c: Vertical(g32)
    c: Coincident(g33,g32)
    c: Horizontal(g33)
    c: Coincident(g34,g33)
    c: Vertical(g34)
    c: Block(g33)
    c: Coincident(g35,g13)
    c: Coincident(g35,g34)
    c: Horizontal(g35)
    c: Coincident(g36,g13)
    c: Coincident(g36,g20)
    c: Coincident(g37,g20)
    c: Coincident(g37,g30)
    c: Block(g30)
    c: Coincident(g38,g1)
    c: Coincident(g38,g2)
    c: Coincident(g39,g1)
    c: Coincident(g39,g2)
    c: Coincident(g40,g3)
    c: Coincident(g40,g4)
    c: Coincident(g41,g3)
    c: Coincident(g41,g4)
    c: Coincident(g42,g5)
    c: Coincident(g42,g6)
    c: Coincident(g43,g5)
    c: Coincident(g43,g6)
    c: Coincident(g44,g7)
    c: Coincident(g44,g8)
    c: Coincident(g45,g7)
    c: Coincident(g45,g8)
    c: Distance(g30) = 256
    c: Distance(g33) = 100
FEATURE [Part::Extrusion] Extrude002
  Base = -> Sketch001
  Dir = (1,0,0)
  DirMode = 2
  FaceMakerClass = Part::FaceMakerBullseye
  LengthFwd = 8
  LengthRev = 0
  Solid = true
  Symmetric = false
FEATURE [Sketcher::SketchObject] Sketch002
  FullyConstrained = true
  sketch-geometry (20):
    g0: LineSegment StartX=-2.77179 StartY=-200.304 StartZ=0 EndX=5.22821 EndY=-200.304 EndZ=0
    g1: LineSegment StartX=5.22821 StartY=-200.304 StartZ=0 EndX=5.22821 EndY=-197.304 EndZ=0
    g2: LineSegment StartX=-2.77179 StartY=-200.304 StartZ=0 EndX=-2.77179 EndY=-197.304 EndZ=0
    g3: LineSegment StartX=5.22821 StartY=-197.304 StartZ=0 EndX=8.22821 EndY=-197.304 EndZ=0
    g4: LineSegment StartX=-2.77179 StartY=-197.304 StartZ=0 EndX=-5.77179 EndY=-197.304 EndZ=0
    g5: LineSegment StartX=19.2282 StartY=-203.304 StartZ=0 EndX=19.2282 EndY=-206.304 EndZ=0
    g6: LineSegment StartX=-16.7718 StartY=-203.304 StartZ=0 EndX=-16.7718 EndY=-206.304 EndZ=0
    g7: LineSegment StartX=-16.7718 StartY=-206.304 StartZ=0 EndX=19.2282 EndY=-206.304 EndZ=0
    g8: Circle CenterX=-16.7718 CenterY=-203.304 CenterZ=0 NormalX=0 NormalY=0 NormalZ=1 AngleXU=0 Radius=1
    g9: Circle CenterX=-5.77179 CenterY=-203.304 CenterZ=0 NormalX=0 NormalY=0 NormalZ=1 AngleXU=0 Radius=1
    g10: Circle CenterX=-5.77179 CenterY=-197.304 CenterZ=0 NormalX=0 NormalY=0 NormalZ=1 AngleXU=0 Radius=1
    g11: BSplineCurve PolesCount=3 KnotsCount=2 Degree=2 IsPeriodic=0
    g12: GeomPoint X=-16.7718 Y=-203.304 Z=0
    g13: GeomPoint X=-5.77179 Y=-197.304 Z=0
    g14: Circle CenterX=19.2282 CenterY=-203.304 CenterZ=0 NormalX=0 NormalY=0 NormalZ=1 AngleXU=0 Radius=1
    g15: Circle CenterX=8.22821 CenterY=-203.304 CenterZ=0 NormalX=0 NormalY=0 NormalZ=1 AngleXU=0 Radius=1
    g16: Circle CenterX=8.22821 CenterY=-197.304 CenterZ=0 NormalX=0 NormalY=0 NormalZ=1 AngleXU=0 Radius=1
    g17: BSplineCurve PolesCount=3 KnotsCount=2 Degree=2 IsPeriodic=0
    g18: GeomPoint X=19.2282 Y=-203.304 Z=0
    g19: GeomPoint X=8.22821 Y=-197.304 Z=0
  constraints (41):
    c: Horizontal(g0)
    c: Distance(g0) = 8
    c: Coincident(g1,g0)
    c: Vertical(g1)
    c: Distance(g1) = 3
    c: Coincident(g2,g0)
    c: Vertical(g2)
    c: Distance(g2) = 3
    c: Coincident(g3,g1)
    c: Horizontal(g3)
    c: Distance(g3) = 3
    c: Coincident(g4,g2)
    c: Horizontal(g4)
    c: Distance(g4) = 3
    c: Vertical(g5)
    c: Vertical(g6)
    c: Coincident(g7,g6)
    c: Coincident(g7,g5)
    c: Weight(g8) = 1
    c: Equal(g8,g9)
    c: Equal(g8,g10)
    c: Coincident(g11,g4)
    c: InternalAlignment(g8,g11)
    c: InternalAlignment(g9,g11)
    c: InternalAlignment(g10,g11)
    c: InternalAlignment(g12,g11)
    c: InternalAlignment(g13,g11)
    c: Coincident(g17,g5)
    c: Weight(g14) = 1
    c: Equal(g14,g15)
    c: Equal(g14,g16)
    c: Coincident(g17,g3)
    c: InternalAlignment(g14,g17)
    c: InternalAlignment(g15,g17)
    c: InternalAlignment(g16,g17)
    c: InternalAlignment(g18,g17)
    c: InternalAlignment(g19,g17)
    c: Block(g7)
    c: Block(g17)
    c: Block(g11)
    c: Block(g6)
FEATURE [Part::Extrusion] Extrude003
  Base = -> Sketch002
  Dir = (0,0,1)
  DirMode = 2
  FaceMakerClass = Part::FaceMakerBullseye
  LengthFwd = 260
  LengthRev = 0
  Solid = true
  Symmetric = false
FEATURE [Part::Extrusion] Extrude
  Base = -> Sketch
  Dir = (0,0,1)
  DirMode = 2
  FaceMakerClass = Part::FaceMakerBullseye
  LengthFwd = 14
  LengthRev = 0
  Solid = true
  Symmetric = false
